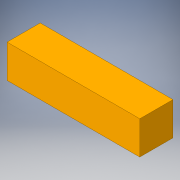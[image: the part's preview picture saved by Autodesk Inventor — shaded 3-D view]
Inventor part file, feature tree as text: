
AUTODESK INVENTOR PART (.ipt)
format: ipt  version: 2016 (Build 200138000, 138)  size: 96,256 bytes
history: native  units: in
note: dims shown in document units (in); Inventor stores cm internally (conversion verified against a paired STEP export)
features: extrude x1, sketch x1
ambient origin geometry x8: Origin, YZ Plane, XZ Plane, XY Plane, X Axis, Y Axis, Z Axis, Center Point
bodies: Solid1 (feature_tree)
feature tree (2):
  extrude  "Extrusion1"  Depth=1.0in
  sketch  "Sketch1"  dims[d0=4.0in d1=1.0in d2=1.0in d3=0.0in]
